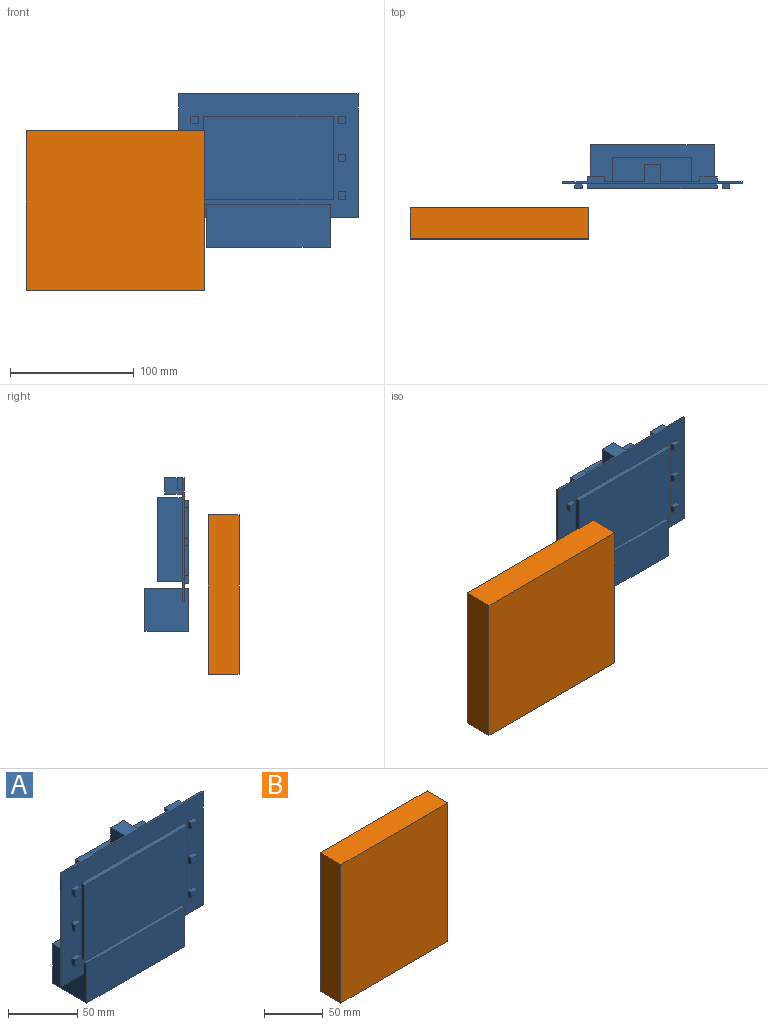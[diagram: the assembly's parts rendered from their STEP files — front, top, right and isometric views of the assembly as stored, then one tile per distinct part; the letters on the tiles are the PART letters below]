
ASSEMBLY  parts=2 mates=1
PART A: 71 faces, bbox 145x35.6x124 mm
  f0: plane 68x64mm, normal (0,1,0), area 507mm2, adj f38,f39,f40,f41,f42,f43,f69,f70
  f1: plane 145x100mm, normal (0,-1,0), area 6128mm2, adj f3,f4,f5,f6,f7,f8,f10,f11
  f2: plane 145x100mm, normal (0,1,0), area 8627mm2, adj f3,f4,f5,f25,f26,f28,f29,f30
  f3: plane 22.5x1.55mm, normal (0,0,-1), area 34.9mm2, adj f1,f2,f4,f37
  f4: plane 100x1.55mm, normal (1,0,0), area 155mm2, adj f1,f2,f3,f5
  f5: plane 145x15.55mm, normal (0,0,1), area 518.7mm2, adj f1,f2,f4,f26,f27,f28,f30,f31
  f6: plane 105x4mm, normal (0,0,1), area 420mm2, adj f1,f8,f9,f47
  f7: plane 105x4mm, normal (0,0,-1), area 420mm2, adj f1,f8,f9,f47
  f8: plane 67.2x4mm, normal (1,0,0), area 268.8mm2, adj f1,f6,f7,f9
  f9: plane 105x67.2mm, normal (0,-1,0), area 7056mm2, adj f6,f7,f8,f47
  f10: plane 6x4mm, normal (0,0,1), area 24mm2, adj f1,f11,f13,f14
  f11: plane 6x4mm, normal (-1,0,0), area 24mm2, adj f1,f10,f12,f14
  f12: plane 6x4mm, normal (0,0,-1), area 24mm2, adj f1,f11,f13,f14
  f13: plane 6x4mm, normal (1,0,0), area 24mm2, adj f1,f10,f12,f14
  f14: plane 6x6mm, normal (0,-1,0), area 36mm2, adj f10,f11,f12,f13
  f15: plane 6x4mm, normal (0,0,1), area 24mm2, adj f1,f16,f18,f19
  f16: plane 6x4mm, normal (-1,0,0), area 24mm2, adj f1,f15,f17,f19
  f17: plane 6x4mm, normal (0,0,-1), area 24mm2, adj f1,f16,f18,f19
  f18: plane 6x4mm, normal (1,0,0), area 24mm2, adj f1,f15,f17,f19
  f19: plane 6x6mm, normal (0,-1,0), area 36mm2, adj f15,f16,f17,f18
  f20: plane 6x4mm, normal (0,0,1), area 24mm2, adj f1,f21,f23,f24
  f21: plane 6x4mm, normal (-1,0,0), area 24mm2, adj f1,f20,f22,f24
  f22: plane 6x4mm, normal (0,0,-1), area 24mm2, adj f1,f21,f23,f24
  f23: plane 6x4mm, normal (1,0,0), area 24mm2, adj f1,f20,f22,f24
  f24: plane 6x6mm, normal (0,-1,0), area 36mm2, adj f20,f21,f22,f23
  f25: plane 14x13mm, normal (0,0,-1), area 182mm2, adj f2,f26,f27,f63
  f26: plane 14x13mm, normal (1,0,0), area 182mm2, adj f2,f5,f25,f27
  f27: plane 13x13mm, normal (0,1,0), area 169mm2, adj f5,f25,f26,f63
  f28: plane 9x4mm, normal (1,0,0), area 36mm2, adj f2,f5,f29,f31
  f29: plane 14x4mm, normal (0,0,-1), area 56mm2, adj f2,f28,f30,f31
  f30: plane 9x4mm, normal (-1,0,0), area 36mm2, adj f2,f5,f29,f31
  f31: plane 14x9mm, normal (0,1,0), area 126mm2, adj f5,f28,f29,f30
  f32: plane 100x30mm, normal (0,0,1), area 3000mm2, adj f2,f33,f37,f68
  f33: plane 100x35mm, normal (0,1,0), area 3500mm2, adj f32,f36,f37,f68
  f34: plane 100x3.45mm, normal (0,0,1), area 345mm2, adj f1,f35,f37,f68
  f35: plane 100x35mm, normal (0,-1,0), area 3500mm2, adj f34,f36,f37,f68
  f36: plane 100x35mm, normal (0,0,-1), area 3500mm2, adj f33,f35,f37,f68
  f37: plane 35x35mm, normal (1,0,0), area 1208mm2, adj f1,f2,f3,f32,f33,f34,f35,f36
  f38: plane 64x20mm, normal (0,0,1), area 1280mm2, adj f0,f2,f39,f69
  f39: plane 68x20mm, normal (1,0,0), area 1360mm2, adj f0,f2,f38,f40
  f40: plane 64x20mm, normal (0,0,-1), area 1280mm2, adj f0,f2,f39,f69
  f41: plane 60.2x18mm, normal (0,0,-1), area 1083.6mm2, adj f0,f42,f44,f70
  f42: plane 63.87x18mm, normal (-1,0,0), area 1149.7mm2, adj f0,f41,f43,f44
  f43: plane 60.2x18mm, normal (0,0,1), area 1083.6mm2, adj f0,f42,f44,f70
  f44: plane 63.87x60.2mm, normal (0,1,0), area 3845mm2, adj f41,f42,f43,f70
  f45: plane 22.5x1.55mm, normal (0,0,-1), area 34.9mm2, adj f1,f2,f46,f68
  f46: plane 100x1.55mm, normal (-1,0,0), area 155mm2, adj f1,f2,f5,f45
  f47: plane 67.2x4mm, normal (-1,0,0), area 268.8mm2, adj f1,f6,f7,f9
  f48: plane 6x4mm, normal (0,0,1), area 24mm2, adj f1,f49,f51,f52
  f49: plane 6x4mm, normal (1,0,0), area 24mm2, adj f1,f48,f50,f52
  f50: plane 6x4mm, normal (0,0,-1), area 24mm2, adj f1,f49,f51,f52
  f51: plane 6x4mm, normal (-1,0,0), area 24mm2, adj f1,f48,f50,f52
  f52: plane 6x6mm, normal (0,-1,0), area 36mm2, adj f48,f49,f50,f51
  f53: plane 6x4mm, normal (0,0,1), area 24mm2, adj f1,f54,f56,f57
  f54: plane 6x4mm, normal (1,0,0), area 24mm2, adj f1,f53,f55,f57
  f55: plane 6x4mm, normal (0,0,-1), area 24mm2, adj f1,f54,f56,f57
  f56: plane 6x4mm, normal (-1,0,0), area 24mm2, adj f1,f53,f55,f57
  f57: plane 6x6mm, normal (0,-1,0), area 36mm2, adj f53,f54,f55,f56
  f58: plane 6x4mm, normal (0,0,1), area 24mm2, adj f1,f59,f61,f62
  f59: plane 6x4mm, normal (1,0,0), area 24mm2, adj f1,f58,f60,f62
  f60: plane 6x4mm, normal (0,0,-1), area 24mm2, adj f1,f59,f61,f62
  f61: plane 6x4mm, normal (-1,0,0), area 24mm2, adj f1,f58,f60,f62
  f62: plane 6x6mm, normal (0,-1,0), area 36mm2, adj f58,f59,f60,f61
  f63: plane 14x13mm, normal (-1,0,0), area 182mm2, adj f2,f5,f25,f27
  f64: plane 9x4mm, normal (-1,0,0), area 36mm2, adj f2,f5,f65,f67
  f65: plane 14x4mm, normal (0,0,-1), area 56mm2, adj f2,f64,f66,f67
  f66: plane 9x4mm, normal (1,0,0), area 36mm2, adj f2,f5,f65,f67
  f67: plane 14x9mm, normal (0,1,0), area 126mm2, adj f5,f64,f65,f66
  f68: plane 35x35mm, normal (-1,0,0), area 1208mm2, adj f1,f2,f32,f33,f34,f35,f36,f45
  f69: plane 68x20mm, normal (-1,0,0), area 1360mm2, adj f0,f2,f38,f40
  f70: plane 63.87x18mm, normal (1,0,0), area 1149.7mm2, adj f0,f41,f43,f44
PART B: 6 faces, bbox 128.6x25x144 mm
  f0: plane 144.02x25mm, normal (-1,0,0), area 3600.5mm2, adj f1,f3,f4,f5
  f1: plane 128.63x25mm, normal (0,0,-1), area 3215.8mm2, adj f0,f2,f4,f5
  f2: plane 144.02x25mm, normal (1,0,0), area 3600.5mm2, adj f1,f3,f4,f5
  f3: plane 128.63x25mm, normal (0,0,1), area 3215.8mm2, adj f0,f2,f4,f5
  f4: plane 144.02x128.63mm, normal (0,-1,0), area 18525.1mm2, adj f0,f1,f2,f3
  f5: plane 144.02x128.63mm, normal (0,1,0), area 18525.1mm2, adj f0,f1,f2,f3
PLACE A t=(-25.66,43.43,28.08)mm
PLACE B rot(axis=(0,1,0),90deg) t=(-221.51,23.99,98.16)mm
MATE parallel B.f3 <-> A.f47  axis (1,0,0) through (-77.5,23.99,98.16)mm
